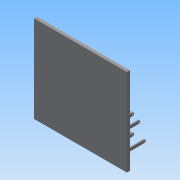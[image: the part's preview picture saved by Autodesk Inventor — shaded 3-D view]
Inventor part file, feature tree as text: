
AUTODESK INVENTOR PART (.ipt)
format: ipt  version: 2015 (Build 190159000, 159)  size: 179,712 bytes
history: native  units: mm
features: extrude x7, sketch x6, projected_geometry x2, other x1, plane x1
ambient origin geometry x8: Origin, YZ Plane, XZ Plane, XY Plane, X Axis, Y Axis, Z Axis, Center Point
bodies: Body1 (feature_tree)
feature tree (17):
  other  "實體1"
  extrude  "擠出1"  Depth=160.0mm
  extrude  "擠出2"  Depth=130.0mm
  extrude  "擠出3"  Depth=5.0mm TaperAngle=0.0deg
  extrude  "擠出4"  Depth=20.4mm
  extrude  "擠出5"  Depth=5.0mm
  plane  "工作平面1"
  sketch  "草圖6"
  extrude  "擠出6"  Depth=2.5mm
  extrude  "擠出7"  Depth=2.0mm TaperAngle=0.0deg
  sketch  "草圖1"
  sketch  "草圖2"
  sketch  "草圖3"
  sketch  "草圖4"
  sketch  "草圖5"
  projected_geometry  "投影迴路1"
  projected_geometry  "投影迴路2"
